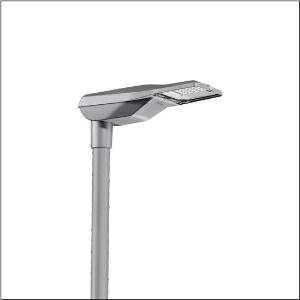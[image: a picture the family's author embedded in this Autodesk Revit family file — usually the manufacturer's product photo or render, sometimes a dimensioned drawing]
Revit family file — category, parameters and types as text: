
# Revit family: streetlight_sl_21_micro___stw1_0a_5xe5e23a08cb_749e
name_source: partatom
category: Lighting Fixtures
units: mm (PartAtom-declared; Revit-internal decimal feet)

## family parameters
Cut with Voids When Loaded = No
Host = Face
Light Source = No
Part Type = Normal
Room Calculation Point = No
Round Connector Dimension = Use Diameter
Shared = No

## types (1)
- --- (1 x LED, 1900 lm, 15.8 W, 2200K)
    Apparent Load = 16 VA
    CIE Flux Codes = 38 75 98 100 100
    Color Rendering = 70
    Color Temperature = 2200K
    Default Elevation = 1800 mm
    Description = Streetlight SL 21 micro, mast luminaire, primary light control with lens, of PMMA, primary optical cover: cover, of toughened safety glass, transparent, light distribution: STW1.0a, light emission: direct distribution, primary light characteristic: asymmetric, installation type: side-entry, post-top, LED, 3G 1.5mm², High Power LED, rated luminous flux: 1.900lm, luminous efficacy: 120lm/W, light colour: 722, colour temperature: 2200K, control: flexible luminous flux parameterisation, time-dependent luminous flux control, constant luminous flux control, overheat protection, mains connection: 230..240V, AC, 50/60Hz, connection cable pre-assembled, cable length: 5,5m, wiring characteristics: H07RN-F, start of lifetime: 16W, end of service life: 16W, reduction: 8W, luminaire housing, of diecast aluminium, powder-coated, Siteco® metallic grey (DB 702S), corrosivity category C5 mid according to DIN EN ISO 12944, please order mast flange separately, inclination adjustable: 0°, 5°, 10°, 15°, sealing non-destructively replaceable, multi-level sealing system, length: 528mm, width: 235mm, height: 110mm, mast flange for spigot size: 42mm (side-entry): 5XC10008XM4, 60/48mm (side-entry/post-top): 5XC10108XM2, 76/60mm (side-entry/post-top): 5XC10108XM1, protection rating (complete): IP66, insulation class (complete): insulation class II (safety insulation), certification: CE, ENEC, ENEC+, VDE, impact resistance: IK09, permissible operating ambient temperature for outdoor applications: -40..+50°C, standard-compliant lighting for roads and squares, packaging unit: 1 piece

Light Distribution: STW1.0a
    Height = 110 mm
    Lamp = 1 x LED
    Lamp Light Flux = 1900 lm
    Lamp Power = 15.8 W
    Lamp count = 1
    Length = 528 mm
    Luminous efficacy = 120 lm/W
    Manufacturer = Siteco
    ModVariant = No
    Model = 5XE5E23A08CB
    Number of Poles = 1
    OnlyDefault = Yes
    Power Factor = 1
    Product Name = Streetlight SL 21 micro | STW1.0a
    Product group = mast luminaire | pylon top
    ProductGroupID = 6100
    Protection Class = Protection class II
    Protection Degree = IP 66
    RLX_Detail_Level = 1
    RLX_Emergency_Light_Flux = 0 lm
    RLX_Emergency_Type = 0
    RLX_Emergency_Type_DB = No
    RlxData = <blob elided: 97841 chars, md5=7a4e927a>
    Socket = socket
    Standby Power = 0 W
    System Light Flux = 1900 lm
    System Power = 16 W
    Type Comments = factory setting: luminous flux: 100 % | Output Level: 100 % | 300 mA
    Type Image = l_1006881.jpg
    URL = http://relux.com
    VarID = @adj_105361
    Voltage = 0 V
    Weight = 0.00 kg
    Width = 235 mm

## geometry (parser evidence)
native form markers: Blend x4, Sweep x10
no freeform markers — native parametric forms only
